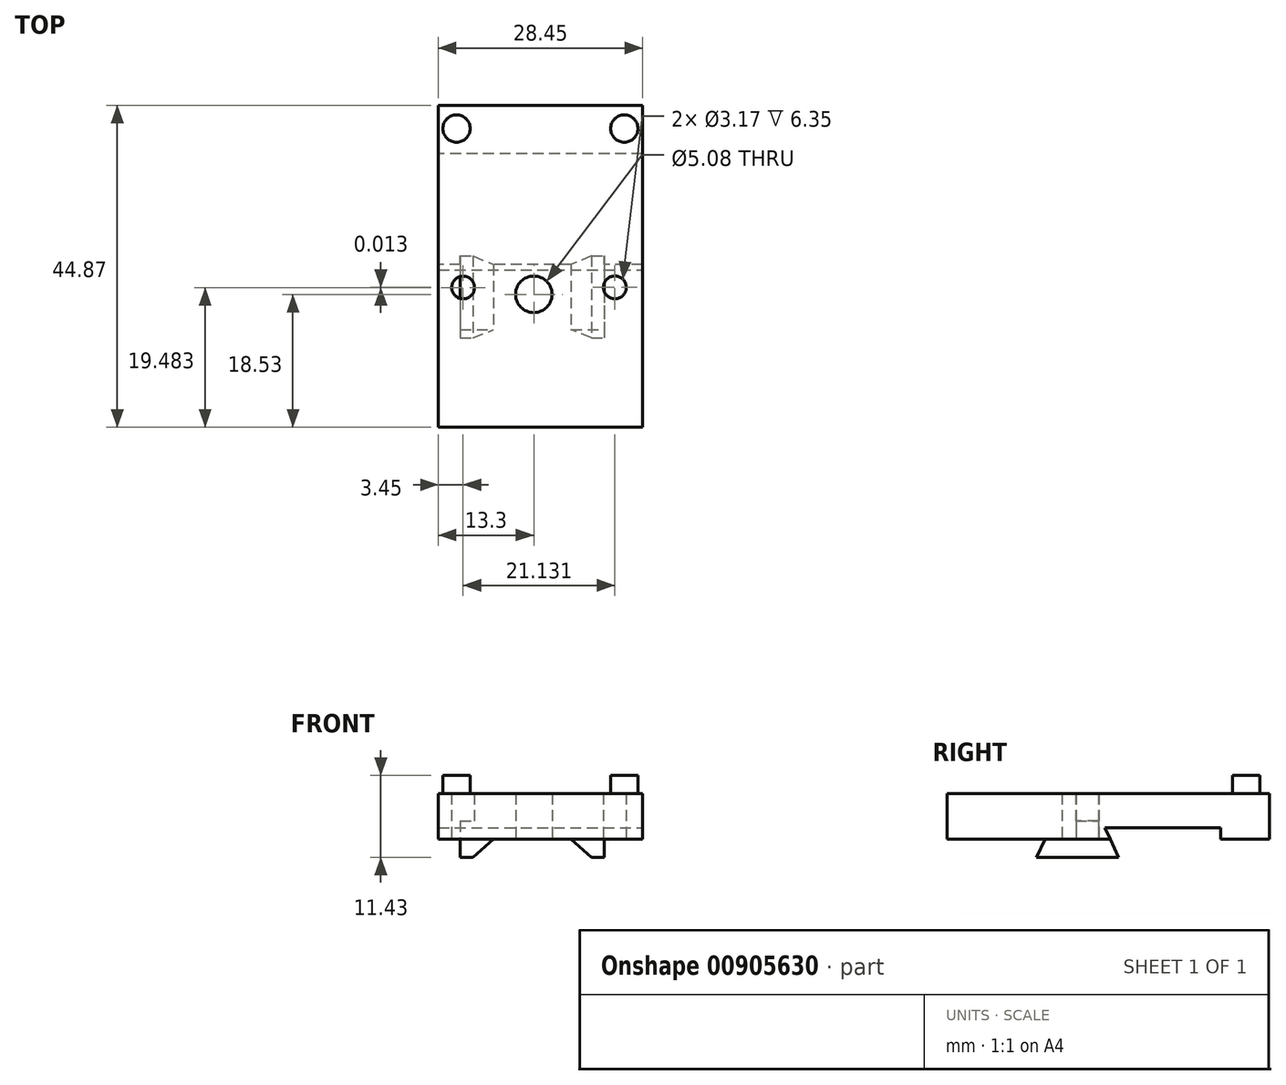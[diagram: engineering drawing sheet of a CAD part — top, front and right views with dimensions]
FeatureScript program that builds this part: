
annotation { "Feature Type Name" : "Feature", "Feature Type Description" : "" }
export const myFeature = defineFeature(function(context is Context, id is Id, definition is map)
    precondition{}
    {
        {
            var Q0;
            Q0=qCreatedBy(makeId("Top.planeOp"),FACE);
            var sketch = newSketch(context, id + "F0", { "sketchPlane" : qUnion([Q0])});
            skLineSegment(sketch, "E0.bottom", {"start": v(-35.35, 39.72) * mm, "end": v(-63.8, 39.72) * mm});
            skLineSegment(sketch, "E0.top", {"start": v(-35.35, 84.59) * mm, "end": v(-63.8, 84.59) * mm});
            skLineSegment(sketch, "E0.left", {"start": v(-35.35, 39.72) * mm, "end": v(-35.35, 84.59) * mm});
            skLineSegment(sketch, "E0.right", {"start": v(-63.8, 39.72) * mm, "end": v(-63.8, 84.59) * mm});
            skCircle(sketch, "E1", {"center": v(-60.35, 59.2) * mm, "radius": 1.59 * mm});
            skCircle(sketch, "E2", {"center": v(-39.22, 59.22) * mm, "radius": 1.59 * mm});
            skCircle(sketch, "E3", {"center": v(-50.5, 58.25) * mm, "radius": 2.54 * mm});
            skSolve(sketch);
        }
        {
            var Q0;
            Q0 = qSketchRegion(id + "F0", true);
            extrude(context, id + "F1", {"entities" : qUnion([Q0]), "depth" : 6.35 * mm, "offsetDistance" : 25.4 * mm});
        }
        {
            var Q0;
            Q0=makeQuery(id+"F1.opExtrude","SWEPT_FACE",FACE,{"disambiguationData":[OSD([sQuery(id+"F0.wireOp",EDGE,"E0.bottom")])]});
            var sketch = newSketch(context, id + "F2", { "sketchPlane" : qUnion([Q0])});
            skLineSegment(sketch, "E4", {"start": v(-60.73, 0) * mm, "end": v(-60.73, -2.54) * mm});
            skLineSegment(sketch, "E5", {"start": v(-60.73, -2.54) * mm, "end": v(-58.96, -2.54) * mm});
            skLineSegment(sketch, "E6", {"start": v(-58.96, -2.54) * mm, "end": v(-56.12, 0) * mm});
            skLineSegment(sketch, "E7", {"start": v(-40.68, 0) * mm, "end": v(-40.68, -2.54) * mm});
            skLineSegment(sketch, "E8", {"start": v(-40.68, -2.54) * mm, "end": v(-42.46, -2.54) * mm});
            skLineSegment(sketch, "E9", {"start": v(-42.46, -2.54) * mm, "end": v(-45.3, 0) * mm});
            skSolve(sketch);
        }
        {
            var Q0;
            Q0 = qSketchRegion(id + "F2", true);
            var Q1;
            {var subQ0=sQuery(id+"F2.wireOp",EDGE,"E4");Q1=makeQuery(id+"F2.imprint","IMPRINT",FACE,{"disambiguationData":[TD([[makeQuery(id+"F2.imprint","IMPRINT",EDGE,{"derivedFrom":subQ0}),1.0]])]});}
            var Q2;
            {var subQ0=sQuery(id+"F2.wireOp",EDGE,"E7");Q2=makeQuery(id+"F2.imprint","IMPRINT",FACE,{"disambiguationData":[TD([[makeQuery(id+"F2.imprint","IMPRINT",EDGE,{"derivedFrom":subQ0}),-1.0]])]});}
            extrude(context, id + "F3", {"entities" : qUnion([Q0, Q1, Q2]), "operationType" : NewBodyOperationType.ADD, "depth" : -38.1 * mm, "offsetDistance" : 25.4 * mm});
        }
        {
            var Q0;
            Q0=makeQuery(id+"F1.opExtrude","SWEPT_FACE",FACE,{"disambiguationData":[OSD([sQuery(id+"F0.wireOp",EDGE,"E0.left")])]});
            var sketch = newSketch(context, id + "F4", { "sketchPlane" : qUnion([Q0])});
            skLineSegment(sketch, "E10.bottom", {"start": v(77.82, -2.54) * mm, "end": v(63.59, -2.54) * mm});
            skLineSegment(sketch, "E10.top", {"start": v(77.82, 1.59) * mm, "end": v(61.66, 1.59) * mm});
            skLineSegment(sketch, "E10.left", {"start": v(77.82, -2.54) * mm, "end": v(77.82, 1.59) * mm});
            skLineSegment(sketch, "E11.bottom", {"start": v(39.72, -2.54) * mm, "end": v(52.16, -2.54) * mm});
            skLineSegment(sketch, "E11.top", {"start": v(39.72, 0) * mm, "end": v(53.34, 0) * mm});
            skLineSegment(sketch, "E11.left", {"start": v(39.72, -2.54) * mm, "end": v(39.72, 0) * mm});
            skLineSegment(sketch, "E12", {"start": v(63.59, -2.54) * mm, "end": v(61.66, 1.59) * mm});
            skLineSegment(sketch, "E13", {"start": v(52.16, -2.54) * mm, "end": v(53.34, 0) * mm});
            skSolve(sketch);
        }
        {
            var Q0;
            Q0 = qSketchRegion(id + "F4", true);
            extrude(context, id + "F5", {"entities" : qUnion([Q0]), "operationType" : NewBodyOperationType.REMOVE, "oppositeDirection" : true, "depth" : 50.8 * mm, "offsetDistance" : 25.4 * mm});
        }
        {
            var Q0;
            Q0=makeQuery(id+"F1.opExtrude","CAP_FACE",FACE,{"disambiguationData":[OSD([sQuery(id+"F0.wireOp",EDGE,"E0.bottom"),sQuery(id+"F0.wireOp",EDGE,"E0.top"),sQuery(id+"F0.wireOp",EDGE,"E0.left"),sQuery(id+"F0.wireOp",EDGE,"E0.right"),sQuery(id+"F0.wireOp",EDGE,"kvBDbbFB-BRii-HYf1-kqZV-HnobOCWYthpv"),sQuery(id+"F0.wireOp",EDGE,"W63sQeVA-Vb2m-V6vr-oigr-5icxakYBt2L3"),sQuery(id+"F0.wireOp",EDGE,"rmjhgAVl-Hoq5-EFCT-gYS6-zwX85jTinCZA")])],"isStart":false});
            var sketch = newSketch(context, id + "F6", { "sketchPlane" : qUnion([Q0])});
            skCircle(sketch, "E14", {"center": v(-61.26, 81.35) * mm, "radius": 1.9 * mm});
            skCircle(sketch, "E15", {"center": v(-37.9, 81.35) * mm, "radius": 1.9 * mm});
            skSolve(sketch);
        }
        {
            var Q0;
            Q0=makeQuery(id+"F6.imprint","IMPRINT",FACE,{"disambiguationData":[TD([[makeQuery(id+"F6.imprint","IMPRINT",EDGE,{"derivedFrom":sQuery(id+"F6.wireOp",EDGE,"E14")}),1.0]])]});
            var Q1;
            Q1=makeQuery(id+"F6.imprint","IMPRINT",FACE,{"disambiguationData":[TD([[makeQuery(id+"F6.imprint","IMPRINT",EDGE,{"derivedFrom":sQuery(id+"F6.wireOp",EDGE,"E15")}),1.0]])]});
            var Q2;
            {var subQ0=sQuery(id+"F0.wireOp",EDGE,"E0.bottom");var subQ1=makeQuery(id+"F1.opExtrude","CAP_EDGE",EDGE,{"disambiguationData":[OSD([subQ0])],"isStart":true});Q2=makeQuery(id+"F3.opExtrude","SWEPT_FACE",FACE,{"disambiguationData":[OSD([subQ0]),TDD([makeQuery(id+"F2.imprint","IMPRINT",EDGE,{"disambiguationData":[TD([[makeQuery(id+"F2.imprint","INTERSECT",VERTEX,{"derivedFrom":[subQ1,sQuery(id+"F2.wireOp",EDGE,"E4")]}),1.0]])],"derivedFrom":subQ1})])]});}
            extrude(context, id + "F7", {"entities" : qUnion([Q0, Q1, Q2]), "operationType" : NewBodyOperationType.ADD, "depth" : 2.54 * mm, "offsetDistance" : 25.4 * mm});
        }
    });
